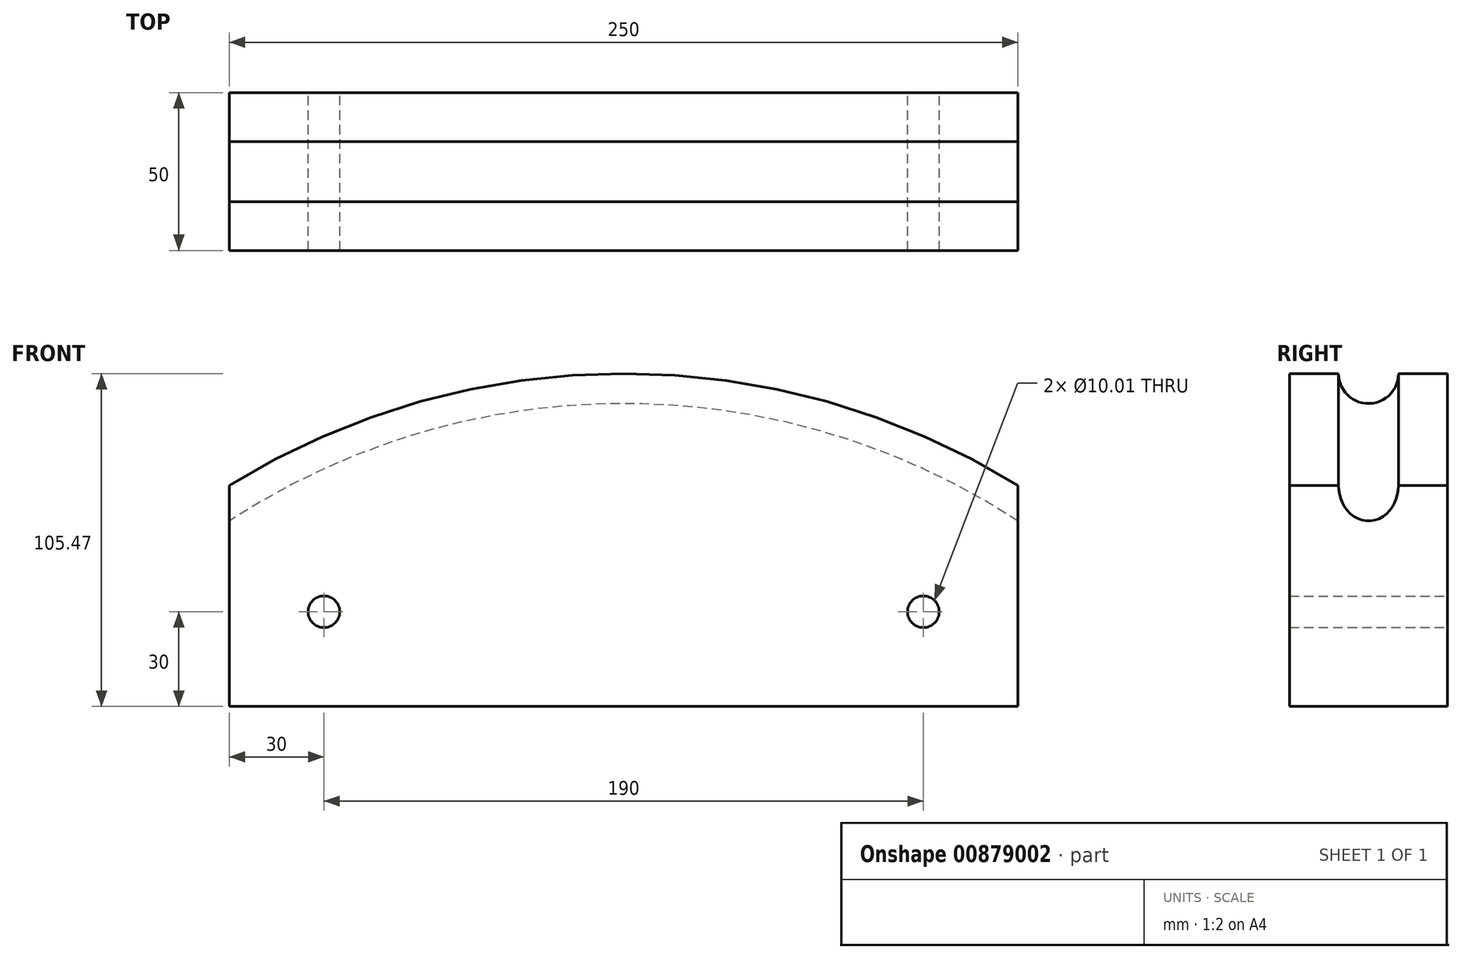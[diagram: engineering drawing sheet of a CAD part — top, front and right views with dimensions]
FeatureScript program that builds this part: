
annotation { "Feature Type Name" : "Feature", "Feature Type Description" : "" }
export const myFeature = defineFeature(function(context is Context, id is Id, definition is map)
    precondition{}
    {
        {
            var Q0;
            Q0=qCreatedBy(makeId("Front.planeOp"),FACE);
            var sketch = newSketch(context, id + "F0", { "sketchPlane" : qUnion([Q0])});
            skLineSegment(sketch, "E0", {"start": v(0, 0) * mm, "end": v(-125, 0) * mm});
            skLineSegment(sketch, "E1", {"start": v(-125, 0) * mm, "end": v(-125, 70) * mm});
            skLineSegment(sketch, "E2", {"start": v(0, 0) * mm, "end": v(0, 105.47) * mm, "construction": true});
            skLineSegment(sketch, "E3.MirrorCS", {"start": v(0, 0) * mm, "end": v(125, 0) * mm});
            skLineSegment(sketch, "E4.MirrorCS", {"start": v(125, 0) * mm, "end": v(125, 70) * mm});
            skArc(sketch, "E5", {"start": v(125, 70) * mm, "mid": v(0, 105.47) * mm, "end": v(-125, 70) * mm});
            skLineSegment(sketch, "E6", {"start": v(-125, 0) * mm, "end": v(-95, 0) * mm});
            skLineSegment(sketch, "E7", {"start": v(-95, 0) * mm, "end": v(-95, 30) * mm, "construction": true});
            skLineSegment(sketch, "E8", {"start": v(-95, 30) * mm, "end": v(-125, 30) * mm, "construction": true});
            skLineSegment(sketch, "E9.MirrorCS", {"start": v(95, 0) * mm, "end": v(95, 30) * mm, "construction": true});
            skLineSegment(sketch, "E10.MirrorCS", {"start": v(95, 30) * mm, "end": v(125, 30) * mm, "construction": true});
            skSolve(sketch);
        }
        {
            var Q0;
            Q0=makeQuery(id+"F0.imprint","IMPRINT",FACE,{"disambiguationData":[TD([[makeQuery(id+"F0.imprint","IMPRINT",EDGE,{"derivedFrom":sQuery(id+"F0.wireOp",EDGE,"E0")}),-1.0]])]});
            extrude(context, id + "F1", {"entities" : qUnion([Q0]), "depth" : 50 * mm, "offsetDistance" : 25 * mm});
        }
        {
            var Q0;
            Q0=sQuery(id+"F0.wireOp",VERTEX,"E9.MirrorCS.end");
            var Q1;
            Q1=sQuery(id+"F0.wireOp",VERTEX,"E7.end");
            var Q2;
            Q2=makeQuery(id+"F1.opExtrude","SWEPT_BODY",BODY,{"disambiguationData":[OSD([sQuery(id+"F0.wireOp",EDGE,"E0"),sQuery(id+"F0.wireOp",EDGE,"E1"),sQuery(id+"F0.wireOp",EDGE,"E3.MirrorCS"),sQuery(id+"F0.wireOp",EDGE,"E4.MirrorCS"),sQuery(id+"F0.wireOp",EDGE,"E5"),sQuery(id+"F0.wireOp",EDGE,"E6")])]});
            hole(context, id + "F2", {"style" : HoleStyle.SIMPLE, "endStyle" : HoleEndStyle.THROUGH, "oppositeDirection" : true, "holeDiameter" : 10.02 * mm, "majorDiameter" : 12 * mm, "tappedDepth" : 9 * mm, "tapClearance" : 3, "startFromSketch" : true, "locations" : qUnion([Q0, Q1]), "scope" : qUnion([Q2])});
        }
        {
            var Q0;
            Q0=qCreatedBy(makeId("Right.planeOp"),FACE);
            var sketch = newSketch(context, id + "F3", { "sketchPlane" : qUnion([Q0])});
            skPoint(sketch, "E11.0", {"position": v(0, 105.47) * mm});
            skLineSegment(sketch, "E12", {"start": v(0, 105.47) * mm, "end": v(-50, 105.47) * mm});
            skCircle(sketch, "E13", {"center": v(-25, 105.47) * mm, "radius": 9.5 * mm});
            skSolve(sketch);
        }
        {
            var Q0;
            Q0=qCreatedBy(makeId("Front.planeOp"),FACE);
            cPlane(context, id + "F4", {"entities" : qUnion([Q0]), "cplaneType" : CPlaneType.OFFSET, "offset" : 25 * mm, "width" : 150 * mm, "height" : 150 * mm});
        }
        {
            var Q0;
            Q0=qCreatedBy(id+"F4.planeOp",FACE);
            var sketch = newSketch(context, id + "F5", { "sketchPlane" : qUnion([Q0])});
            skArc(sketch, "E14.0", {"start": v(169.88, 34.16) * mm, "mid": v(2, 105.46) * mm, "end": v(-167.05, 37) * mm});
            skPoint(sketch, "E15.orphan", {"position": v(-125, 70) * mm});
            skPoint(sketch, "E16.orphan", {"position": v(125, 70) * mm});
            skSolve(sketch);
        }
        {
            var Q0;
            {var subQ0=sQuery(id+"F3.wireOp",EDGE,"E13");var subQ1=sQuery(id+"F3.wireOp",EDGE,"E12");var subQ2=makeQuery(id+"F3.imprint","INTERSECT",VERTEX,{"disambiguationData":[OD(0.0)],"derivedFrom":[subQ1,subQ0]});Q0=makeQuery(id+"F3.imprint","IMPRINT",FACE,{"disambiguationData":[TD([[makeQuery(id+"F3.imprint","IMPRINT",EDGE,{"disambiguationData":[TD([[subQ2,1.0]])],"derivedFrom":subQ1}),-1.0]])]});}
            var Q1;
            {var subQ0=sQuery(id+"F3.wireOp",EDGE,"E13");var subQ1=sQuery(id+"F3.wireOp",EDGE,"E12");var subQ2=makeQuery(id+"F3.imprint","INTERSECT",VERTEX,{"disambiguationData":[OD(0.0)],"derivedFrom":[subQ1,subQ0]});Q1=makeQuery(id+"F3.imprint","IMPRINT",FACE,{"disambiguationData":[TD([[makeQuery(id+"F3.imprint","IMPRINT",EDGE,{"disambiguationData":[TD([[subQ2,1.0]])],"derivedFrom":subQ1}),1.0]])]});}
            var Q2;
            Q2=sQuery(id+"F5.wireOp",EDGE,"E14.0");
            sweep(context, id + "F6", {"operationType" : NewBodyOperationType.REMOVE, "profiles" : qUnion([Q0, Q1]), "path" : qUnion([Q2])});
        }
    });
